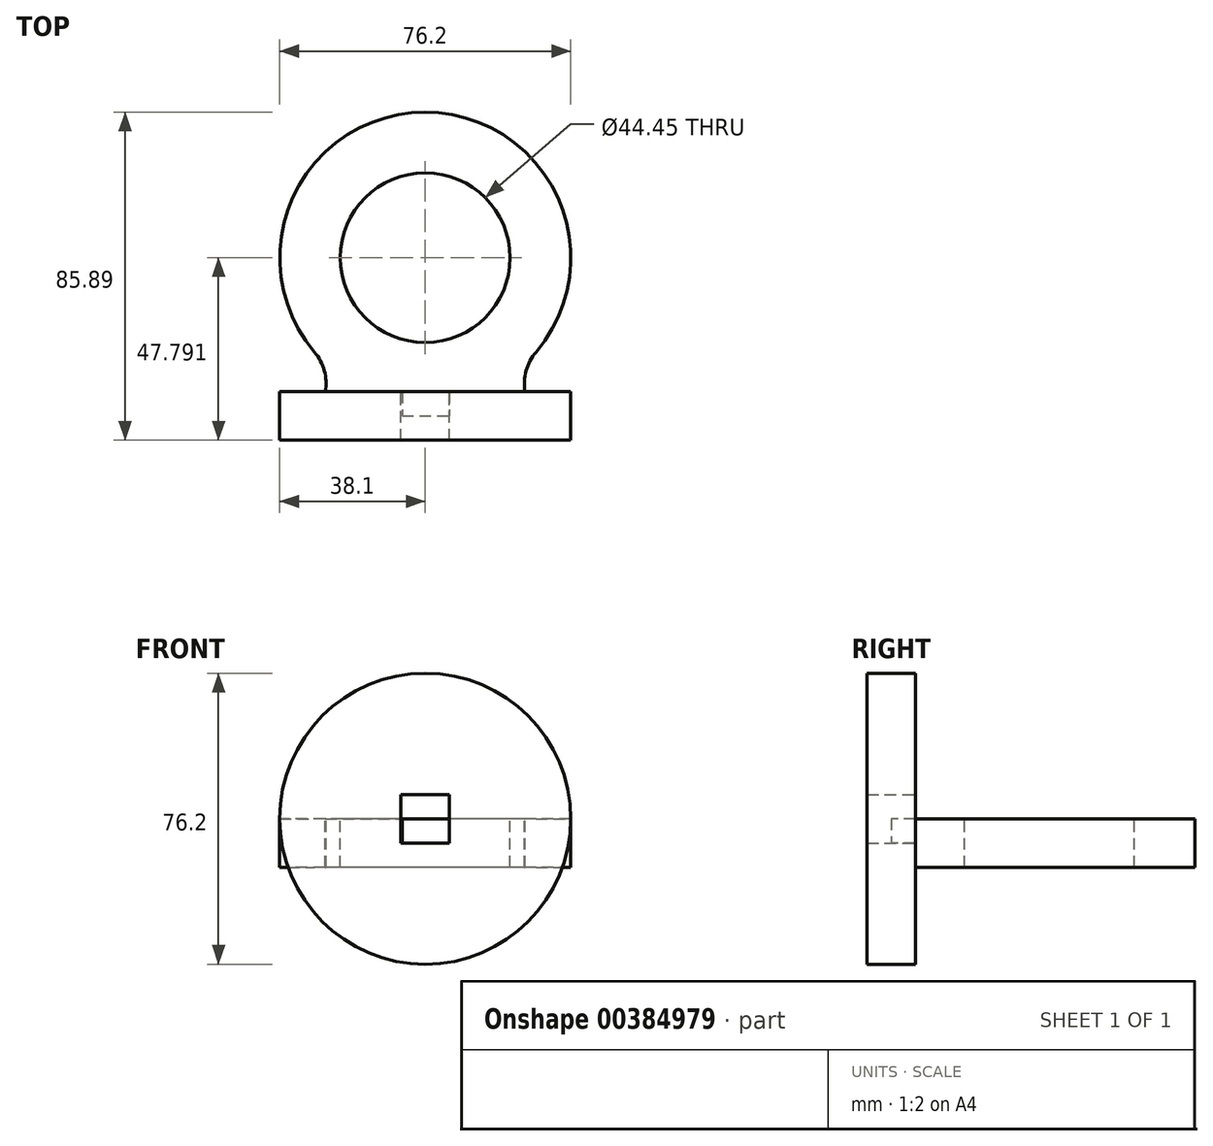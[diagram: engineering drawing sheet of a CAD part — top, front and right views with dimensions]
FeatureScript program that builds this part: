
annotation { "Feature Type Name" : "Feature", "Feature Type Description" : "" }
export const myFeature = defineFeature(function(context is Context, id is Id, definition is map)
    precondition{}
    {
        {
            var Q0;
            Q0=qCreatedBy(makeId("Front.planeOp"),FACE);
            var sketch = newSketch(context, id + "F0", { "sketchPlane" : qUnion([Q0])});
            skCircle(sketch, "E0", {"center": v(0, 0) * mm, "radius": 38.1 * mm});
            skLineSegment(sketch, "E1.bottom", {"start": v(-6.35, 6.35) * mm, "end": v(6.35, 6.35) * mm});
            skLineSegment(sketch, "E1.top", {"start": v(-6.35, -6.35) * mm, "end": v(6.35, -6.35) * mm});
            skLineSegment(sketch, "E1.left", {"start": v(-6.35, 6.35) * mm, "end": v(-6.35, -6.35) * mm});
            skLineSegment(sketch, "E1.right", {"start": v(6.35, 6.35) * mm, "end": v(6.35, -6.35) * mm});
            skLineSegment(sketch, "E2", {"start": v(0, 6.35) * mm, "end": v(0, 0) * mm});
            skLineSegment(sketch, "E3", {"start": v(-6.35, 0) * mm, "end": v(0, 0) * mm});
            skSolve(sketch);
        }
        {
            var Q0;
            Q0 = qSketchRegion(id + "F0", true);
            extrude(context, id + "F1", {"entities" : qUnion([Q0]), "depth" : 12.7 * mm});
        }
        {
            var Q0;
            Q0=qCreatedBy(makeId("Top.planeOp"),FACE);
            var sketch = newSketch(context, id + "F2", { "sketchPlane" : qUnion([Q0])});
            skArc(sketch, "E4", {"start": v(29, 10.38) * mm, "mid": v(0, 73.2) * mm, "end": v(-29, 10.38) * mm});
            skArc(sketch, "E5", {"start": v(-26.14, 0) * mm, "mid": v(-26.42, 5.5) * mm, "end": v(-29, 10.38) * mm});
            skArc(sketch, "E6", {"start": v(29, 10.38) * mm, "mid": v(26.42, 5.5) * mm, "end": v(26.14, 0) * mm});
            skLineSegment(sketch, "E7", {"start": v(-26.14, 0) * mm, "end": v(-6.06, 0) * mm});
            skLineSegment(sketch, "E8", {"start": v(-6.06, 0) * mm, "end": v(-6.06, -6.35) * mm});
            skLineSegment(sketch, "E9", {"start": v(-6.06, -6.35) * mm, "end": v(6.42, -6.35) * mm});
            skLineSegment(sketch, "E10", {"start": v(6.42, -6.35) * mm, "end": v(6.42, 0) * mm});
            skLineSegment(sketch, "E11", {"start": v(6.42, 0) * mm, "end": v(26.14, 0) * mm});
            skCircle(sketch, "E12", {"center": v(0, 35.1) * mm, "radius": 22.23 * mm});
            skSolve(sketch);
        }
        {
            var Q0;
            Q0=makeQuery(id+"F2.imprint","IMPRINT",FACE,{"disambiguationData":[TD([[makeQuery(id+"F2.imprint","IMPRINT",EDGE,{"derivedFrom":sQuery(id+"F2.wireOp",EDGE,"E4")}),1.0]])]});
            extrude(context, id + "F3", {"entities" : qUnion([Q0]), "operationType" : NewBodyOperationType.ADD, "oppositeDirection" : true, "depth" : 12.7 * mm});
        }
    });
